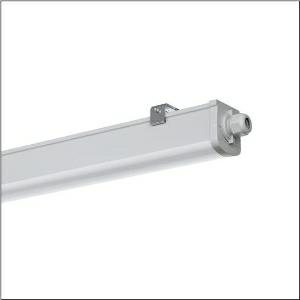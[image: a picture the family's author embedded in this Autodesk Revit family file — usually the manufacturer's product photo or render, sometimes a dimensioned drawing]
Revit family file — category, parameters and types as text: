
# Revit family: monsun_r__31_51fa207p430b_b845
name_source: partatom
category: Lighting Fixtures
units: mm (PartAtom-declared; Revit-internal decimal feet)

## family parameters
Cut with Voids When Loaded = No
Host = Face
Light Source = No
Part Type = Normal
Room Calculation Point = No
Round Connector Dimension = Use Diameter
Shared = No

## types (1)
- Monsun® 31 (1 x LED, 3800 lm, 28 W, 4000K)
    Apparent Load = 28 VA
    CIE Flux Codes = 42 72 91 92 100
    Color Rendering = 80
    Color Temperature = 4000K
    Default Elevation = 1800 mm
    Description = Monsun® 31, damp-proof luminaire, primary optical cover: diffuser, of PC, frosted, light emission: direct distribution, primary light characteristic: symmetric, installation type: surface-mounted, LED, rated luminous flux: 3.800lm, luminous efficacy: 136lm/W, light colour: 840, colour temperature: 4000K, control gear: ON/OFF, with terminal, 3+1-pole, max. 2.5mm², through-wiring: 3x 2.5mm² + 1x 1.5mm², mains connection: 220..240V, AC, 50/60Hz, rated input power: 28W, housing, luminaire housing, of PC, light grey (RAL 7035), length: 1.458mm, width: 68mm, height: 76mm, protection rating (complete): IP66, insulation class (complete): insulation class II (safety insulation), certification: CE, ENEC, UKCA, protection symbol: D, impact resistance: IK08, permissible operating ambient temperature: -20..+40°C, corresponds to IFS (International Featured Standards) requirements for safety and quality in the food industry, contact your sales advisor before using the luminaires in applications with unclear chemical exposure, large temperature fluctuations or condensation-forming humidity, packaging unit: 1 piece
    Height = 77 mm
    Lamp = 1 x LED
    Lamp Light Flux = 3800 lm
    Lamp Power = 28 W
    Lamp count = 1
    Length = 1518 mm
    Luminous efficacy = 136 lm/W
    Manufacturer = Siteco
    ModVariant = No
    Model = 51FA207P430B
    Mounting Place = Ceiling
    Mounting Type = Surface mounted
    Number of Poles = 1
    OnlyDefault = Yes
    Power Factor = 1
    Product Name = Monsun® 31
    Product group = damp-proof luminaire
    ProductGroupID = 301
    Protection Class = Protection class II
    Protection Degree = IP 66
    RLX_Detail_Level = 1
    RLX_Emergency_Light_Flux = 0 lm
    RLX_Emergency_Type = 0
    RLX_Emergency_Type_DB = No
    RlxData = <blob elided: 33081 chars, md5=004f9a43>
    Socket = socket
    Standby Power = 0 W
    System Light Flux = 3800 lm
    System Power = 28 W
    Type Comments = Product without accessories
    Type Image = l_1006174.jpg
    URL = http://relux.com
    VarID = ---
    Voltage = 0 V
    Weight = 0.00 kg
    Width = 69 mm

## geometry (parser evidence)
native form markers: Blend x4, Sweep x13
no freeform markers — native parametric forms only
